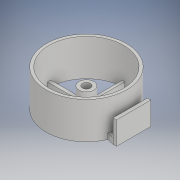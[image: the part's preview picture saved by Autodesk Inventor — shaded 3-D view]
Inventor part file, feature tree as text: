
AUTODESK INVENTOR PART (.ipt)
format: ipt  version: 2019 (Build 230136000, 136)  size: 250,368 bytes
history: native  units: in
note: dims shown in document units (in); Inventor stores cm internally (conversion verified against a paired STEP export)
features: sketch x13, extrude x12, projected_geometry x6
ambient origin geometry x8: Origin, YZ Plane, XZ Plane, XY Plane, X Axis, Y Axis, Z Axis, Center Point
bodies: Solid1 (feature_tree)
feature tree (31):
  extrude  "Extrusion1"  Depth=0.15in
  extrude  "Extrusion2"  Depth=0.1in TaperAngle=0.0deg
  extrude  "Extrusion3"  Depth=0.75in
  sketch  "Sketch6"  dims[d8=0.15in d9=0.25in d10=0.0in]
  extrude  "Extrusion7"  Depth=0.25in TaperAngle=0.0deg
  extrude  "Extrusion9"  Depth=0.875in TaperAngle=0.0deg
  extrude  "Extrusion10"  Depth=0.115in
  extrude  "Extrusion11"  Depth=0.05in
  extrude  "Extrusion12"  Depth=0.115in
  extrude  "Extrusion14"  Depth=0.05in
  extrude  "Extrusion15"  TaperAngle=0.0deg  [1 undecoded]
  extrude  "Extrusion16"  TaperAngle=0.0deg  [1 undecoded]
  extrude  "Extrusion17"  Depth=0.1in
  sketch  "Sketch1"  dims[d0=0.35in d1=0.15in]
  sketch  "Sketch2"  dims[d2=0.78in d3=0.0in d4=0.1in d5=0.0in]
  sketch  "Sketch3"  dims[d6=1.5in d7=0.75in]
  sketch  "Sketch10"  dims[d20=0.5315in d28=0.875in d29=0.0in]
  sketch  "Sketch13"  dims[d32=0.115in d33=0.115in]
  sketch  "Sketch14"  dims[d34=0.0675in d35=0.05in]
  projected_geometry  "Projected Loop9"
  projected_geometry  "Projected Loop10"
  projected_geometry  "Projected Loop11"
  projected_geometry  "Projected Loop12"
  sketch  "Sketch15"  dims[d36=0.115in d37=0.115in]
  sketch  "Sketch16"  dims[d38=0.068in d39=0.05in]
  sketch  "Sketch19"  dims[d40=0.15in d41=0.0in d42=0.0in]
  sketch  "Sketch20"  dims[d43=0.0in d44=0.0in]
  projected_geometry  "Projected Loop13"
  sketch  "Sketch21"  dims[d45=0.1in d46=0.0in d47=3.25in]
  projected_geometry  "Projected Loop14"
  sketch  "Sketch23"  dims[d48=3.5in d49=0.1in d50=0.0in d51=3.25in d52=1.5in d53=0.0in d82=0.25in d83=0.0in d84=0.25in d85=0.0in d86=0.25in d87=0.0in d88=0.75in d89=0.0in]
note: 2 required parameter values undecoded (feature->parameter linkage not recoverable at this tier; creation-order binding heuristic only, values carry confidence <= 0.55)
